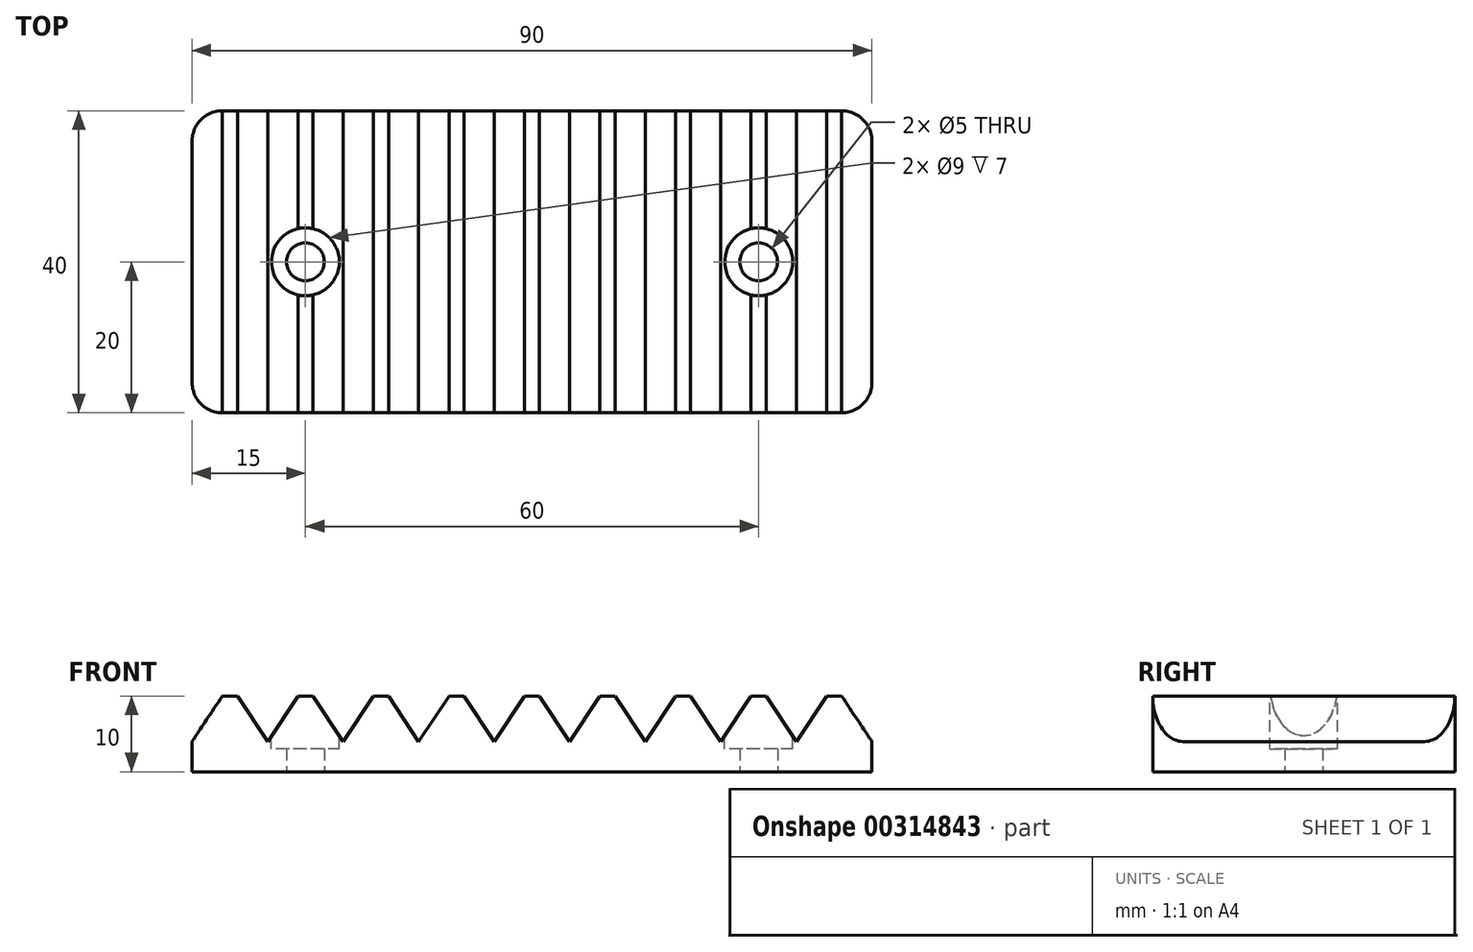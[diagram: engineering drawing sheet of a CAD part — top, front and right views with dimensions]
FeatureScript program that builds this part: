
annotation { "Feature Type Name" : "Feature", "Feature Type Description" : "" }
export const myFeature = defineFeature(function(context is Context, id is Id, definition is map)
    precondition{}
    {
        {
            var Q0;
            Q0=qCreatedBy(makeId("Top.planeOp"),FACE);
            var sketch = newSketch(context, id + "F0", { "sketchPlane" : qUnion([Q0])});
            skLineSegment(sketch, "E0.bottom", {"start": v(0, 0) * mm, "end": v(90, 0) * mm});
            skLineSegment(sketch, "E0.top", {"start": v(0, 40) * mm, "end": v(90, 40) * mm});
            skLineSegment(sketch, "E0.left", {"start": v(0, 0) * mm, "end": v(0, 40) * mm});
            skLineSegment(sketch, "E0.right", {"start": v(90, 0) * mm, "end": v(90, 40) * mm});
            skLineSegment(sketch, "E1", {"start": v(90, 20) * mm, "end": v(75, 20) * mm, "construction": true});
            skCircle(sketch, "E2", {"center": v(15, 20) * mm, "radius": 2.5 * mm});
            skCircle(sketch, "E3", {"center": v(75, 20) * mm, "radius": 2.5 * mm});
            skLineSegment(sketch, "E4.trimOffspring", {"start": v(15, 20) * mm, "end": v(0, 20) * mm, "construction": true});
            skSolve(sketch);
        }
        {
            var Q0;
            Q0 = qSketchRegion(id + "F0", true);
            extrude(context, id + "F1", {"entities" : qUnion([Q0]), "depth" : 10 * mm});
        }
        {
            var Q0;
            Q0=makeQuery(id+"F1.opExtrude","CAP_FACE",FACE,{"disambiguationData":[OSD([sQuery(id+"F0.wireOp",EDGE,"E0.bottom"),sQuery(id+"F0.wireOp",EDGE,"E0.top"),sQuery(id+"F0.wireOp",EDGE,"E0.left"),sQuery(id+"F0.wireOp",EDGE,"E0.right"),sQuery(id+"F0.wireOp",EDGE,"E2"),sQuery(id+"F0.wireOp",EDGE,"E3")])],"isStart":false});
            var sketch = newSketch(context, id + "F2", { "sketchPlane" : qUnion([Q0])});
            skCircle(sketch, "E5", {"center": v(15, 20) * mm, "radius": 4.5 * mm});
            skCircle(sketch, "E6", {"center": v(75, 20) * mm, "radius": 4.5 * mm});
            skSolve(sketch);
        }
        {
            var Q0;
            Q0 = qSketchRegion(id + "F2", true);
            extrude(context, id + "F3", {"entities" : qUnion([Q0]), "operationType" : NewBodyOperationType.REMOVE, "oppositeDirection" : true, "depth" : 7 * mm});
        }
        {
            var Q0;
            Q0=makeQuery(id+"F1.opExtrude","SWEPT_FACE",FACE,{"disambiguationData":[OSD([sQuery(id+"F0.wireOp",EDGE,"E0.bottom")])]});
            var sketch = newSketch(context, id + "F4", { "sketchPlane" : qUnion([Q0])});
            skLineSegment(sketch, "E7", {"start": v(90, 4) * mm, "end": v(0, 4) * mm, "construction": true});
            skLineSegment(sketch, "E8", {"start": v(0, 4) * mm, "end": v(4, 10) * mm});
            skLineSegment(sketch, "E9", {"start": v(4, 10) * mm, "end": v(6, 10) * mm});
            skLineSegment(sketch, "E10", {"start": v(6, 10) * mm, "end": v(10, 4) * mm});
            skLineSegment(sketch, "E11.1.0.0", {"start": v(10, 4) * mm, "end": v(14, 10) * mm});
            skLineSegment(sketch, "E11.1.0.1", {"start": v(14, 10) * mm, "end": v(16, 10) * mm});
            skLineSegment(sketch, "E11.1.0.2", {"start": v(16, 10) * mm, "end": v(20, 4) * mm});
            skLineSegment(sketch, "E11.2.0.0", {"start": v(20, 4) * mm, "end": v(24, 10) * mm});
            skLineSegment(sketch, "E11.2.0.1", {"start": v(24, 10) * mm, "end": v(26, 10) * mm});
            skLineSegment(sketch, "E11.2.0.2", {"start": v(26, 10) * mm, "end": v(30, 4) * mm});
            skLineSegment(sketch, "E11.3.0.0", {"start": v(30, 4) * mm, "end": v(34, 10) * mm});
            skLineSegment(sketch, "E11.3.0.1", {"start": v(34, 10) * mm, "end": v(36, 10) * mm});
            skLineSegment(sketch, "E11.3.0.2", {"start": v(36, 10) * mm, "end": v(40, 4) * mm});
            skLineSegment(sketch, "E11.4.0.0", {"start": v(40, 4) * mm, "end": v(44, 10) * mm});
            skLineSegment(sketch, "E11.4.0.1", {"start": v(44, 10) * mm, "end": v(46, 10) * mm});
            skLineSegment(sketch, "E11.4.0.2", {"start": v(46, 10) * mm, "end": v(50, 4) * mm});
            skLineSegment(sketch, "E11.5.0.0", {"start": v(50, 4) * mm, "end": v(54, 10) * mm});
            skLineSegment(sketch, "E11.5.0.1", {"start": v(54, 10) * mm, "end": v(56, 10) * mm});
            skLineSegment(sketch, "E11.5.0.2", {"start": v(56, 10) * mm, "end": v(60, 4) * mm});
            skLineSegment(sketch, "E11.6.0.0", {"start": v(60, 4) * mm, "end": v(64, 10) * mm});
            skLineSegment(sketch, "E11.6.0.1", {"start": v(64, 10) * mm, "end": v(66, 10) * mm});
            skLineSegment(sketch, "E11.6.0.2", {"start": v(66, 10) * mm, "end": v(70, 4) * mm});
            skLineSegment(sketch, "E11.7.0.0", {"start": v(70, 4) * mm, "end": v(74, 10) * mm});
            skLineSegment(sketch, "E11.7.0.1", {"start": v(74, 10) * mm, "end": v(76, 10) * mm});
            skLineSegment(sketch, "E11.7.0.2", {"start": v(76, 10) * mm, "end": v(80, 4) * mm});
            skLineSegment(sketch, "E11.8.0.0", {"start": v(80, 4) * mm, "end": v(84, 10) * mm});
            skLineSegment(sketch, "E11.8.0.1", {"start": v(84, 10) * mm, "end": v(86, 10) * mm});
            skLineSegment(sketch, "E11.8.0.2", {"start": v(86, 10) * mm, "end": v(90, 4) * mm});
            skLineSegment(sketch, "E11.direction1", {"start": v(0, 4) * mm, "end": v(10, 4) * mm, "construction": true});
            skLineSegment(sketch, "E12", {"start": v(0, 4) * mm, "end": v(0, 10) * mm});
            skLineSegment(sketch, "E13", {"start": v(0, 10) * mm, "end": v(90, 10) * mm});
            skLineSegment(sketch, "E14", {"start": v(90, 10) * mm, "end": v(90, 4) * mm});
            skSolve(sketch);
        }
        {
            var Q0;
            Q0 = qSketchRegion(id + "F4", true);
            extrude(context, id + "F5", {"entities" : qUnion([Q0]), "operationType" : NewBodyOperationType.REMOVE, "endBound" : BoundingType.THROUGH_ALL, "oppositeDirection" : true, "depth" : 25 * mm});
        }
        {
            var Q0;
            Q0=makeQuery(id+"F1.opExtrude","SWEPT_EDGE",EDGE,{"disambiguationData":[OSD([sQuery(id+"F0.wireOp",EDGE,"E0.bottom"),sQuery(id+"F0.wireOp",EDGE,"E0.left")])]});
            var Q1;
            Q1=makeQuery(id+"F1.opExtrude","SWEPT_EDGE",EDGE,{"disambiguationData":[OSD([sQuery(id+"F0.wireOp",EDGE,"E0.top"),sQuery(id+"F0.wireOp",EDGE,"E0.left")])]});
            var Q2;
            Q2=makeQuery(id+"F1.opExtrude","SWEPT_EDGE",EDGE,{"disambiguationData":[OSD([sQuery(id+"F0.wireOp",EDGE,"E0.bottom"),sQuery(id+"F0.wireOp",EDGE,"E0.right")])]});
            var Q3;
            Q3=makeQuery(id+"F1.opExtrude","SWEPT_EDGE",EDGE,{"disambiguationData":[OSD([sQuery(id+"F0.wireOp",EDGE,"E0.top"),sQuery(id+"F0.wireOp",EDGE,"E0.right")])]});
            fillet(context, id + "F6", {"entities" : qUnion([Q0, Q1, Q2, Q3]), "radius" : 4 * mm, "tangentPropagation" : true, "allowEdgeOverflow" : false});
        }
    });
